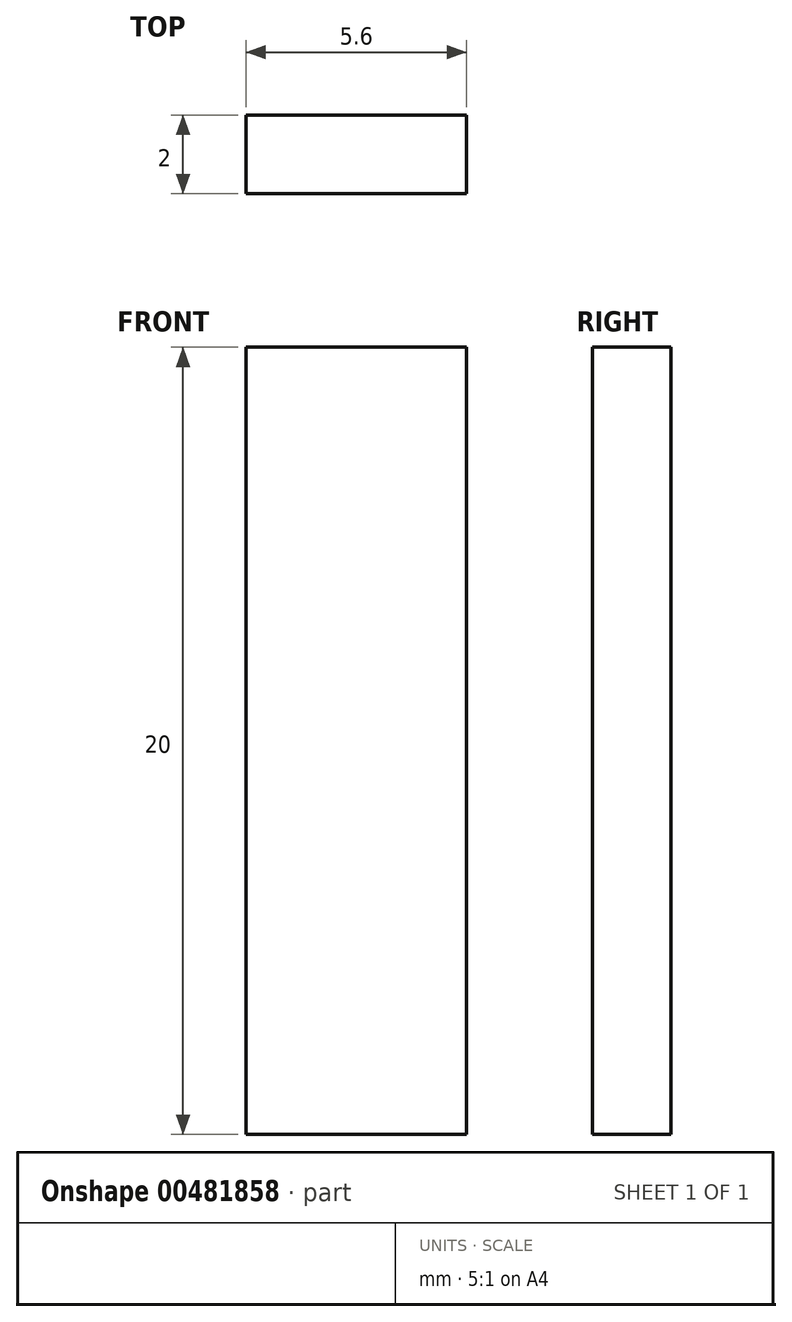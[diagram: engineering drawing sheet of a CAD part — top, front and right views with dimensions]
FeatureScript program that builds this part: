
annotation { "Feature Type Name" : "Feature", "Feature Type Description" : "" }
export const myFeature = defineFeature(function(context is Context, id is Id, definition is map)
    precondition{}
    {
        {
            var Q0;
            Q0=qCreatedBy(makeId("Top.planeOp"),FACE);
            var sketch = newSketch(context, id + "F0", { "sketchPlane" : qUnion([Q0])});
            skLineSegment(sketch, "E0.bottom", {"start": v(2.8, -1) * mm, "end": v(-2.8, -1) * mm});
            skLineSegment(sketch, "E0.top", {"start": v(2.8, 1) * mm, "end": v(-2.8, 1) * mm});
            skLineSegment(sketch, "E0.left", {"start": v(2.8, -1) * mm, "end": v(2.8, 1) * mm});
            skLineSegment(sketch, "E0.right", {"start": v(-2.8, -1) * mm, "end": v(-2.8, 1) * mm});
            skPoint(sketch, "E0.middle", {"position": v(0, 0) * mm});
            skLineSegment(sketch, "E1.bottom", {"start": v(-2.8, 1) * mm, "end": v(-2, 1) * mm});
            skLineSegment(sketch, "E1.top", {"start": v(-2.8, 13) * mm, "end": v(-2, 13) * mm});
            skLineSegment(sketch, "E1.left", {"start": v(-2.8, 1) * mm, "end": v(-2.8, 13) * mm});
            skLineSegment(sketch, "E1.right", {"start": v(-2, 1) * mm, "end": v(-2, 13) * mm});
            skLineSegment(sketch, "E2.bottom", {"start": v(2.8, 1) * mm, "end": v(2, 1) * mm});
            skLineSegment(sketch, "E2.top", {"start": v(2.8, 9) * mm, "end": v(2, 9) * mm});
            skLineSegment(sketch, "E2.left", {"start": v(2.8, 1) * mm, "end": v(2.8, 9) * mm});
            skLineSegment(sketch, "E2.right", {"start": v(2, 1) * mm, "end": v(2, 9) * mm});
            skPoint(sketch, "E3", {"position": v(2, 1) * mm});
            skPoint(sketch, "E4", {"position": v(-2, 1) * mm});
            skSolve(sketch);
        }
        {
            var Q0;
            Q0=makeQuery(id+"F0.imprint","IMPRINT",FACE,{"disambiguationData":[TD([[makeQuery(id+"F0.imprint","IMPRINT",EDGE,{"derivedFrom":sQuery(id+"F0.wireOp",EDGE,"E1.bottom")}),1.0]])]});
            var Q1;
            Q1=makeQuery(id+"F0.imprint","IMPRINT",FACE,{"disambiguationData":[TD([[makeQuery(id+"F0.imprint","IMPRINT",EDGE,{"derivedFrom":sQuery(id+"F0.wireOp",EDGE,"E0.bottom")}),-1.0]])]});
            var Q2;
            Q2=makeQuery(id+"F0.imprint","IMPRINT",FACE,{"disambiguationData":[TD([[makeQuery(id+"F0.imprint","IMPRINT",EDGE,{"derivedFrom":sQuery(id+"F0.wireOp",EDGE,"E2.bottom")}),-1.0]])]});
            extrude(context, id + "F1", {"entities" : qUnion([Q0, Q1, Q2]), "depth" : 20 * mm});
        }
    });
